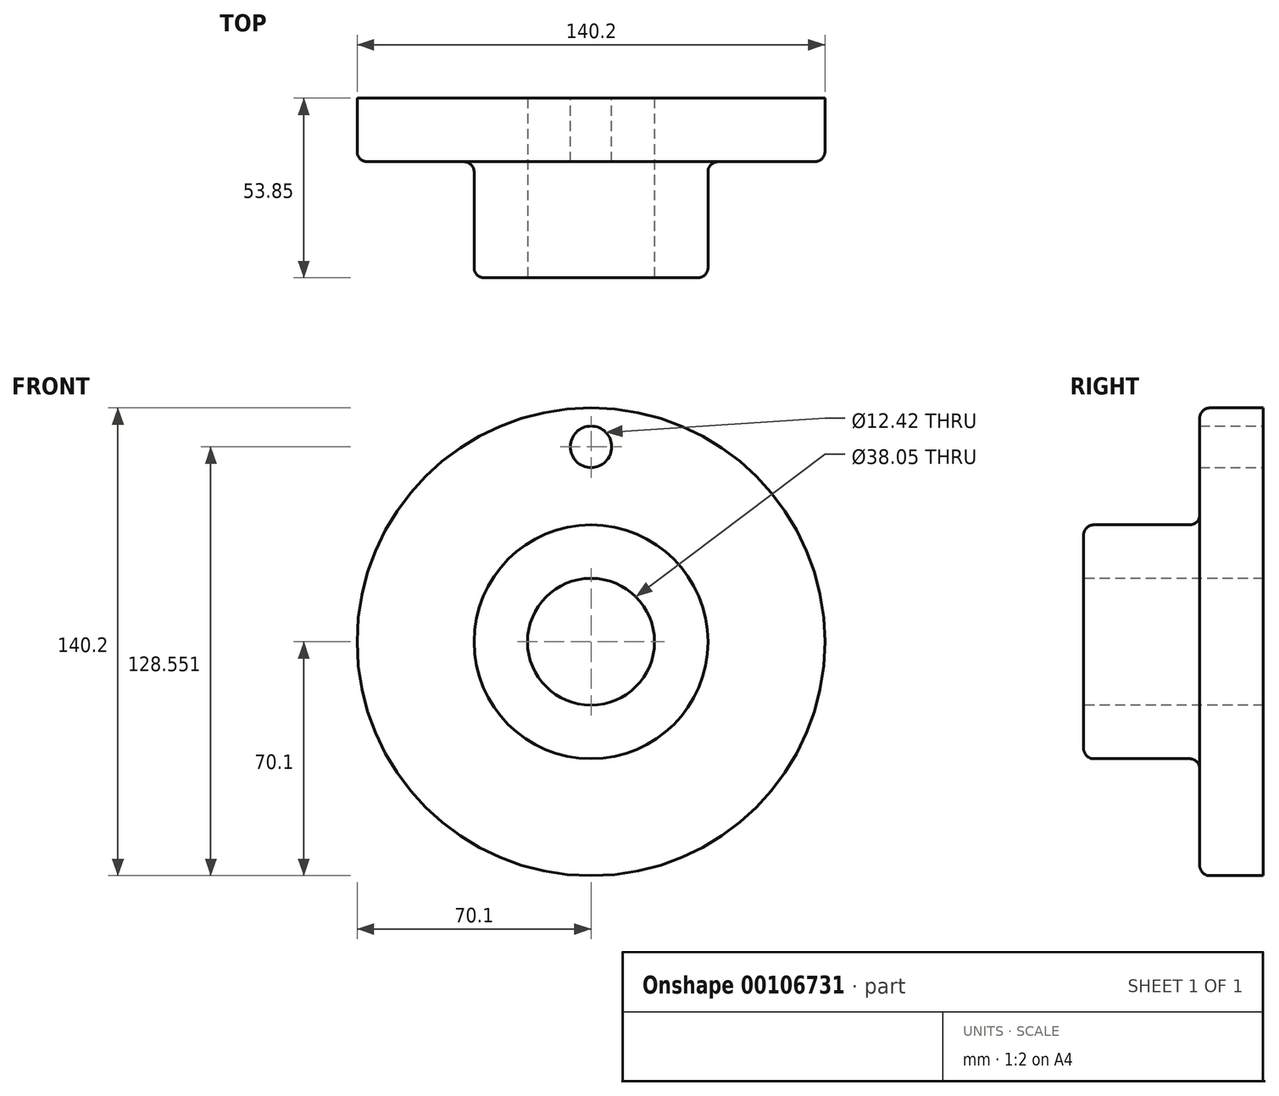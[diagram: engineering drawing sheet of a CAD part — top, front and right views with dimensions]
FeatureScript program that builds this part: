
annotation { "Feature Type Name" : "Feature", "Feature Type Description" : "" }
export const myFeature = defineFeature(function(context is Context, id is Id, definition is map)
    precondition{}
    {
        {
            var Q0;
            Q0=qCreatedBy(makeId("Right.planeOp"),FACE);
            var sketch = newSketch(context, id + "F0", { "sketchPlane" : qUnion([Q0])});
            skLineSegment(sketch, "E0.bottom", {"start": v(0, 0) * mm, "end": v(-19.05, 0) * mm});
            skLineSegment(sketch, "E0.top", {"start": v(0, 70.1) * mm, "end": v(-16, 70.1) * mm});
            skLineSegment(sketch, "E0.left", {"start": v(0, 0) * mm, "end": v(0, 70.1) * mm});
            skLineSegment(sketch, "E0.right", {"start": v(-19.05, 0) * mm, "end": v(-19.05, 67.06) * mm});
            skPoint(sketch, "E1.visualSharp", {"position": v(-19.05, 70.1) * mm});
            skArc(sketch, "E1.filletArc", {"start": v(-16, 70.1) * mm, "mid": v(-18.16, 69.21) * mm, "end": v(-19.05, 67.06) * mm});
            skSolve(sketch);
        }
        {
            var Q0;
            Q0 = qSketchRegion(id + "F0", true);
            var Q1;
            Q1=sQuery(id+"F0.wireOp",EDGE,"E0.bottom");
            revolve(context, id + "F1", {"entities" : qUnion([Q0]), "axis" : qUnion([Q1]), "revolveType" : RevolveType.FULL});
        }
        {
            var Q0;
            Q0=qCreatedBy(makeId("Front.planeOp"),FACE);
            var sketch = newSketch(context, id + "F2", { "sketchPlane" : qUnion([Q0])});
            skCircle(sketch, "E2", {"center": v(0, 58.45) * mm, "radius": 6.2 * mm});
            skSolve(sketch);
        }
        {
            var Q0;
            Q0 = qSketchRegion(id + "F2", true);
            extrude(context, id + "F3", {"entities" : qUnion([Q0]), "operationType" : NewBodyOperationType.REMOVE, "depth" : 53.85 * mm});
        }
        {
            var Q0;
            Q0=qCreatedBy(makeId("Right.planeOp"),FACE);
            var sketch = newSketch(context, id + "F4", { "sketchPlane" : qUnion([Q0])});
            skLineSegment(sketch, "E3.bottom", {"start": v(0, 0) * mm, "end": v(-53.85, 0) * mm});
            skLineSegment(sketch, "E3.top", {"start": v(0, 35.05) * mm, "end": v(-50.8, 35.05) * mm});
            skLineSegment(sketch, "E3.left", {"start": v(0, 0) * mm, "end": v(0, 35.05) * mm});
            skLineSegment(sketch, "E3.right", {"start": v(-53.85, 0) * mm, "end": v(-53.85, 32) * mm});
            skPoint(sketch, "E4.visualSharp", {"position": v(-53.85, 35.05) * mm});
            skArc(sketch, "E4.filletArc", {"start": v(-50.8, 35.05) * mm, "mid": v(-52.96, 34.16) * mm, "end": v(-53.85, 32) * mm});
            skSolve(sketch);
        }
        {
            var Q0;
            Q0 = qSketchRegion(id + "F4", true);
            var Q1;
            Q1=sQuery(id+"F4.wireOp",EDGE,"E3.bottom");
            revolve(context, id + "F5", {"operationType" : NewBodyOperationType.ADD, "entities" : qUnion([Q0]), "axis" : qUnion([Q1]), "revolveType" : RevolveType.FULL});
        }
        {
            var Q0;
            Q0=qCreatedBy(makeId("Right.planeOp"),FACE);
            var sketch = newSketch(context, id + "F6", { "sketchPlane" : qUnion([Q0])});
            skLineSegment(sketch, "E5.bottom", {"start": v(0, 0) * mm, "end": v(-53.85, 0) * mm});
            skLineSegment(sketch, "E5.top", {"start": v(0, 19.02) * mm, "end": v(-53.85, 19.02) * mm});
            skLineSegment(sketch, "E5.left", {"start": v(0, 0) * mm, "end": v(0, 19.02) * mm});
            skLineSegment(sketch, "E5.right", {"start": v(-53.85, 0) * mm, "end": v(-53.85, 19.02) * mm});
            skSolve(sketch);
        }
        {
            var Q0;
            Q0 = qSketchRegion(id + "F6", true);
            var Q1;
            Q1=sQuery(id+"F6.wireOp",EDGE,"E5.bottom");
            revolve(context, id + "F7", {"operationType" : NewBodyOperationType.REMOVE, "entities" : qUnion([Q0]), "axis" : qUnion([Q1]), "revolveType" : RevolveType.FULL, "oppositeDirection" : true});
        }
        {
            var Q0;
            Q0=makeQuery(id+"F5.boolean.opBoolean","INTERSECT",EDGE,{"derivedFrom":[makeQuery(id+"F1.opRevolve","SWEPT_FACE",FACE,{"disambiguationData":[OSD([sQuery(id+"F0.wireOp",EDGE,"E0.right")])]}),makeQuery(id+"F5.opRevolve","SWEPT_FACE",FACE,{"disambiguationData":[OSD([sQuery(id+"F4.wireOp",EDGE,"E3.top")])]})]});
            fillet(context, id + "F8", {"entities" : qUnion([Q0]), "radius" : 3.05 * mm, "tangentPropagation" : true, "allowEdgeOverflow" : false});
        }
    });
